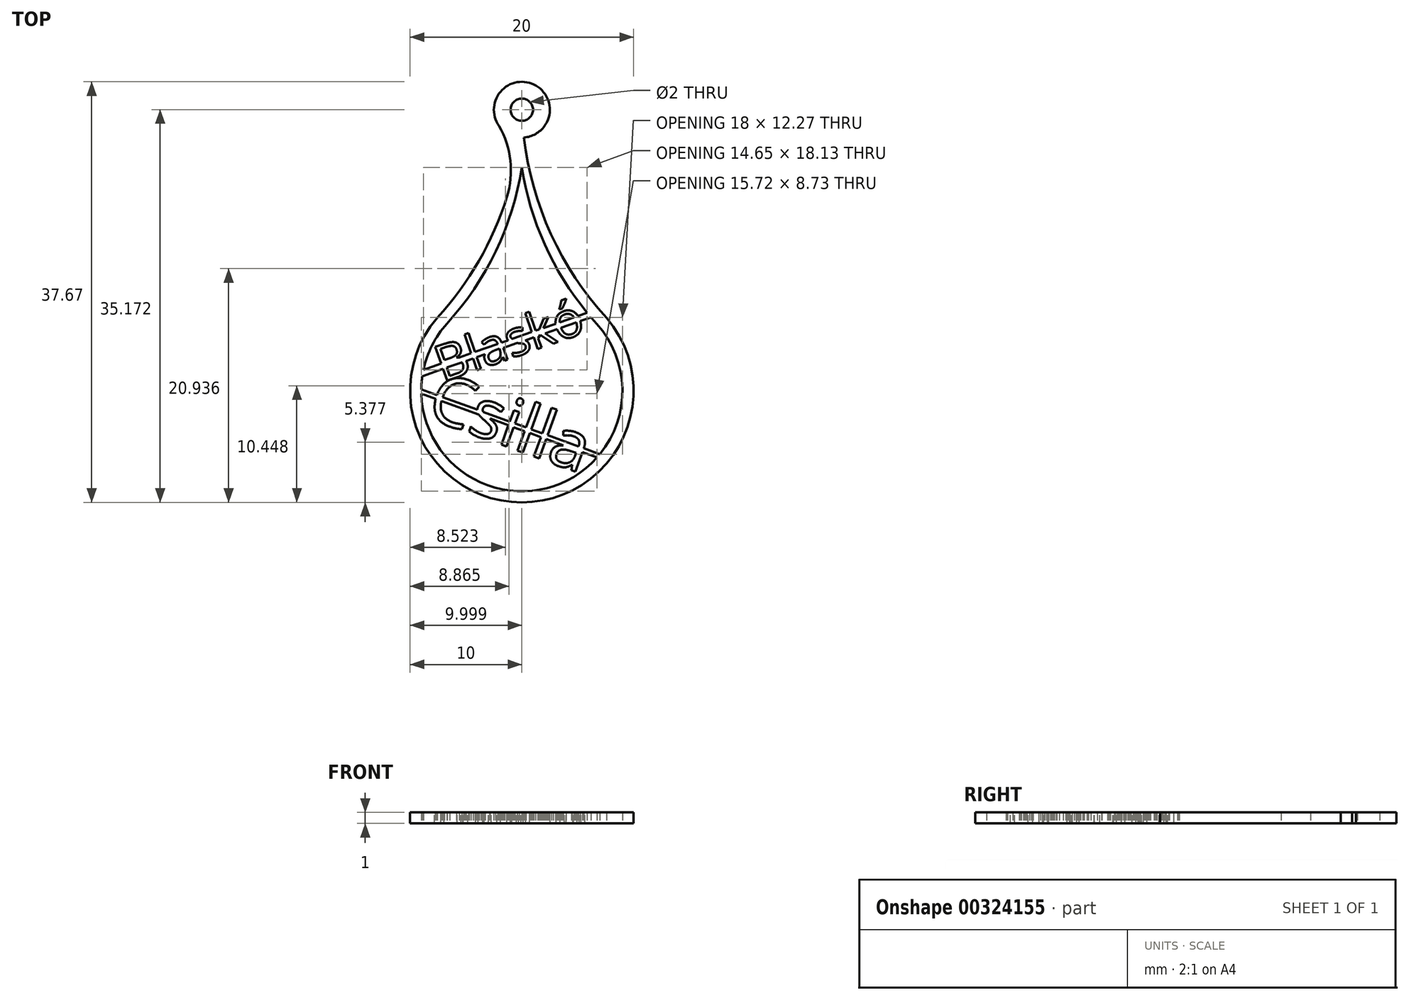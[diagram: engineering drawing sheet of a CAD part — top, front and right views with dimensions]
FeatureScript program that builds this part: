
annotation { "Feature Type Name" : "Feature", "Feature Type Description" : "" }
export const myFeature = defineFeature(function(context is Context, id is Id, definition is map)
    precondition{}
    {
        {
            var Q0;
            Q0=qCreatedBy(makeId("Top.planeOp"),FACE);
            var sketch = newSketch(context, id + "F0", { "sketchPlane" : qUnion([Q0])});
            skArc(sketch, "E0", {"start": v(-6.7, 6) * mm, "mid": v(-8.22, -3.67) * mm, "end": v(0, -9) * mm});
            skArc(sketch, "E1", {"start": v(-7.57, 6.53) * mm, "mid": v(-9.1, -4.16) * mm, "end": v(0, -10) * mm});
            skArc(sketch, "E2", {"start": v(-7.57, 6.53) * mm, "mid": v(-2.31, 14.71) * mm, "end": v(-0.05, 24.17) * mm});
            skLineSegment(sketch, "E3", {"start": v(0, 26.17) * mm, "end": v(0, -10) * mm, "construction": true});
            skArc(sketch, "E4", {"start": v(-6.7, 6) * mm, "mid": v(-2.33, 12.5) * mm, "end": v(0, 20) * mm});
            skArc(sketch, "E5.MirrorCS", {"start": v(0, 25.17) * mm, "mid": v(-0.01, 25.67) * mm, "end": v(-0.01, 26.17) * mm});
            skPoint(sketch, "E6", {"position": v(-8.16, 3.8) * mm});
            skLineSegment(sketch, "E7", {"start": v(0, 0) * mm, "end": v(-8.16, 3.8) * mm, "construction": true});
            skPoint(sketch, "E8.MirrorCS.end.orphan", {"position": v(0, 20) * mm});
            skPoint(sketch, "E9.MirrorCS.end.orphan", {"position": v(0, -9) * mm});
            skPoint(sketch, "E10.MirrorCS.end.orphan", {"position": v(0, -10) * mm});
            skArc(sketch, "E11.MirrorCS", {"start": v(6.7, 6) * mm, "mid": v(2.33, 12.5) * mm, "end": v(0, 20) * mm});
            skArc(sketch, "E12.MirrorCS", {"start": v(7.57, 6.53) * mm, "mid": v(1.93, 15.64) * mm, "end": v(-0.01, 26.17) * mm});
            skArc(sketch, "E13.MirrorCS", {"start": v(6.7, 6) * mm, "mid": v(8.22, -3.67) * mm, "end": v(0, -9) * mm});
            skArc(sketch, "E14.MirrorCS", {"start": v(7.57, 6.53) * mm, "mid": v(9.1, -4.16) * mm, "end": v(0, -10) * mm});
            skLineSegment(sketch, "E15", {"start": v(0, 0) * mm, "end": v(7.1, -10.14) * mm, "construction": true});
            skPoint(sketch, "E16", {"position": v(5.16, -7.37) * mm});
            skLineSegment(sketch, "E17", {"start": v(0, 0) * mm, "end": v(7.3, 12.66) * mm, "construction": true});
            skPoint(sketch, "E18", {"position": v(4.81, 8.33) * mm});
            skText(sketch, "E19", { "text": "Blaskó", "fontName": "OpenSans-Regular.ttf"});
            skText(sketch, "E20", { "text": "Csilla", "fontName": "OpenSans-Regular.ttf"});
            skLineSegment(sketch, "E21", {"start": v(0, 0) * mm, "end": v(-15.9, -4.26) * mm, "construction": true});
            skPoint(sketch, "E22", {"position": v(-8.7, -2.33) * mm});
            skLineSegment(sketch, "E23", {"start": v(-7.63, 2.28) * mm, "end": v(5.34, 6.81) * mm});
            skLineSegment(sketch, "E24", {"start": v(5.34, 6.81) * mm, "end": v(5.85, 7) * mm});
            skLineSegment(sketch, "E25", {"start": v(-7.63, 2.28) * mm, "end": v(-8.8, 1.87) * mm});
            skLineSegment(sketch, "E26", {"start": v(-8.9, 1.3) * mm, "end": v(6.2, 6.58) * mm});
            skLineSegment(sketch, "E27", {"start": v(-7.94, -0.26) * mm, "end": v(5.92, -5.3) * mm});
            skLineSegment(sketch, "E28", {"start": v(5.92, -5.3) * mm, "end": v(6.98, -5.69) * mm});
            skLineSegment(sketch, "E29", {"start": v(-7.94, -0.26) * mm, "end": v(-9, 0.13) * mm});
            skLineSegment(sketch, "E30", {"start": v(-9, -0.26) * mm, "end": v(6.73, -5.98) * mm});
            skCircle(sketch, "E31", {"center": v(0, 25.17) * mm, "radius": 1 * mm});
            skCircle(sketch, "E32", {"center": v(0, 25.17) * mm, "radius": 2.5 * mm});
            skArc(sketch, "E33", {"start": v(2.24, 24.06) * mm, "mid": v(1.06, 20.82) * mm, "end": v(1.33, 17.37) * mm});
            skArc(sketch, "E34.MirrorCS", {"start": v(-2.24, 24.06) * mm, "mid": v(-1.06, 20.82) * mm, "end": v(-1.33, 17.37) * mm});
            skArc(sketch, "E35.trimOffspring", {"start": v(0, 25.17) * mm, "mid": v(0.01, 25.67) * mm, "end": v(0.01, 26.17) * mm});
            skPoint(sketch, "E36.orphan", {"position": v(0, 27) * mm});
            skArc(sketch, "E37.trimOffspring", {"start": v(0, 27) * mm, "mid": v(0, 27) * mm, "end": v(0, 27) * mm});
            const initialGuessF0  = {"E19": [-0.0071, 0.00076, 0.94407, 0.32975, 0.00322], "E20": [-0.0087, -0.00233, 0.9397, -0.34202, 0.00441]};
            skSetInitialGuess(sketch, initialGuessF0);
            skSolve(sketch);
        }
        {
            var Q0;
            Q0=makeQuery(id+"F0.imprint","IMPRINT",FACE,{"disambiguationData":[TD([[makeQuery(id+"F0.imprint","IMPRINT",EDGE,{"derivedFrom":sQuery(id+"F0.wireOp",EDGE,"E0")}),-1.0]])]});
            var Q1;
            Q1=makeQuery(id+"F0.imprint","IMPRINT",FACE,{"disambiguationData":[TD([[makeQuery(id+"F0.imprint","IMPRINT",EDGE,{"derivedFrom":sQuery(id+"F0.wireOp",EDGE,"E19.sketch_text.stroke-56")}),-1.0]])]});
            var Q2;
            Q2=makeQuery(id+"F0.imprint","IMPRINT",FACE,{"disambiguationData":[TD([[makeQuery(id+"F0.imprint","IMPRINT",EDGE,{"derivedFrom":sQuery(id+"F0.wireOp",EDGE,"E19.sketch_text.stroke-81")}),-1.0]])]});
            var Q3;
            Q3=makeQuery(id+"F0.imprint","IMPRINT",FACE,{"disambiguationData":[TD([[makeQuery(id+"F0.imprint","IMPRINT",EDGE,{"derivedFrom":sQuery(id+"F0.wireOp",EDGE,"E19.sketch_text.stroke-96")}),-1.0]])]});
            var Q4;
            Q4=makeQuery(id+"F0.imprint","IMPRINT",FACE,{"disambiguationData":[TD([[makeQuery(id+"F0.imprint","IMPRINT",EDGE,{"derivedFrom":sQuery(id+"F0.wireOp",EDGE,"E19.sketch_text.stroke-113")}),-1.0]])]});
            var Q5;
            Q5=makeQuery(id+"F0.imprint","IMPRINT",FACE,{"disambiguationData":[TD([[makeQuery(id+"F0.imprint","IMPRINT",EDGE,{"derivedFrom":sQuery(id+"F0.wireOp",EDGE,"E19.sketch_text.stroke-29")}),-1.0]])]});
            var Q6;
            Q6=makeQuery(id+"F0.imprint","IMPRINT",FACE,{"disambiguationData":[TD([[makeQuery(id+"F0.imprint","IMPRINT",EDGE,{"derivedFrom":sQuery(id+"F0.wireOp",EDGE,"E19.sketch_text.stroke-25")}),-1.0]])]});
            var Q7;
            Q7=makeQuery(id+"F0.imprint","IMPRINT",FACE,{"disambiguationData":[TD([[makeQuery(id+"F0.imprint","IMPRINT",EDGE,{"derivedFrom":sQuery(id+"F0.wireOp",EDGE,"E19.sketch_text.stroke-0")}),-1.0]])]});
            var Q8;
            Q8=makeQuery(id+"F0.imprint","IMPRINT",FACE,{"disambiguationData":[TD([[makeQuery(id+"F0.imprint","IMPRINT",EDGE,{"derivedFrom":sQuery(id+"F0.wireOp",EDGE,"E20.sketch_text.stroke-0")}),-1.0]])]});
            var Q9;
            Q9=makeQuery(id+"F0.imprint","IMPRINT",FACE,{"disambiguationData":[TD([[makeQuery(id+"F0.imprint","IMPRINT",EDGE,{"derivedFrom":sQuery(id+"F0.wireOp",EDGE,"E20.sketch_text.stroke-15")}),-1.0]])]});
            var Q10;
            Q10=makeQuery(id+"F0.imprint","IMPRINT",FACE,{"disambiguationData":[TD([[makeQuery(id+"F0.imprint","IMPRINT",EDGE,{"derivedFrom":sQuery(id+"F0.wireOp",EDGE,"E20.sketch_text.stroke-44")}),-1.0]])]});
            var Q11;
            Q11=makeQuery(id+"F0.imprint","IMPRINT",FACE,{"disambiguationData":[TD([[makeQuery(id+"F0.imprint","IMPRINT",EDGE,{"derivedFrom":sQuery(id+"F0.wireOp",EDGE,"E20.sketch_text.stroke-52")}),-1.0]])]});
            var Q12;
            Q12=makeQuery(id+"F0.imprint","IMPRINT",FACE,{"disambiguationData":[TD([[makeQuery(id+"F0.imprint","IMPRINT",EDGE,{"derivedFrom":sQuery(id+"F0.wireOp",EDGE,"E20.sketch_text.stroke-40")}),-1.0]])]});
            var Q13;
            Q13=makeQuery(id+"F0.imprint","IMPRINT",FACE,{"disambiguationData":[TD([[makeQuery(id+"F0.imprint","IMPRINT",EDGE,{"derivedFrom":sQuery(id+"F0.wireOp",EDGE,"E20.sketch_text.stroke-56")}),-1.0]])]});
            var Q14;
            Q14=makeQuery(id+"F0.imprint","IMPRINT",FACE,{"disambiguationData":[TD([[makeQuery(id+"F0.imprint","IMPRINT",EDGE,{"derivedFrom":sQuery(id+"F0.wireOp",EDGE,"E20.sketch_text.stroke-60")}),-1.0]])]});
            var Q15;
            {var subQ0=sQuery(id+"F0.wireOp",EDGE,"E20.sketch_text.stroke-26");Q15=makeQuery(id+"F0.imprint","IMPRINT",FACE,{"disambiguationData":[TD([[makeQuery(id+"F0.imprint","IMPRINT",EDGE,{"derivedFrom":subQ0}),1.0]])]});}
            var Q16;
            {var subQ0=sQuery(id+"F0.wireOp",EDGE,"E29");Q16=makeQuery(id+"F0.imprint","IMPRINT",FACE,{"disambiguationData":[TD([[makeQuery(id+"F0.imprint","IMPRINT",EDGE,{"derivedFrom":subQ0}),1.0]])]});}
            var Q17;
            {var subQ5=sQuery(id+"F0.wireOp",EDGE,"E20.sketch_text.stroke-2");var subQ6=sQuery(id+"F0.wireOp",EDGE,"E20.sketch_text.stroke-1");var subQ7=makeQuery(id+"F0.imprint","INTERSECT",VERTEX,{"derivedFrom":[subQ6,subQ5]});Q17=makeQuery(id+"F0.imprint","IMPRINT",FACE,{"disambiguationData":[TD([[makeQuery(id+"F0.imprint","IMPRINT",EDGE,{"disambiguationData":[TD([[subQ7,1.0]])],"derivedFrom":subQ6}),-1.0]])]});}
            var Q18;
            {var subQ0=sQuery(id+"F0.wireOp",EDGE,"E20.sketch_text.stroke-3");Q18=makeQuery(id+"F0.imprint","IMPRINT",FACE,{"disambiguationData":[TD([[makeQuery(id+"F0.imprint","IMPRINT",EDGE,{"derivedFrom":subQ0}),-1.0]])]});}
            var Q19;
            {var subQ5=sQuery(id+"F0.wireOp",EDGE,"E20.sketch_text.stroke-26");Q19=makeQuery(id+"F0.imprint","IMPRINT",FACE,{"disambiguationData":[TD([[makeQuery(id+"F0.imprint","IMPRINT",EDGE,{"derivedFrom":subQ5}),-1.0]])]});}
            var Q20;
            {var subQ6=sQuery(id+"F0.wireOp",EDGE,"E20.sketch_text.stroke-28");Q20=makeQuery(id+"F0.imprint","IMPRINT",FACE,{"disambiguationData":[TD([[makeQuery(id+"F0.imprint","IMPRINT",EDGE,{"derivedFrom":subQ6}),-1.0]])]});}
            var Q21;
            {var subQ6=sQuery(id+"F0.wireOp",EDGE,"E20.sketch_text.stroke-37");Q21=makeQuery(id+"F0.imprint","IMPRINT",FACE,{"disambiguationData":[TD([[makeQuery(id+"F0.imprint","IMPRINT",EDGE,{"derivedFrom":subQ6}),1.0]])]});}
            var Q22;
            {var subQ0=sQuery(id+"F0.wireOp",EDGE,"E30");var subQ1=sQuery(id+"F0.wireOp",EDGE,"E20.sketch_text.stroke-41");var subQ2=makeQuery(id+"F0.imprint","INTERSECT",VERTEX,{"derivedFrom":[subQ1,subQ0]});Q22=makeQuery(id+"F0.imprint","IMPRINT",FACE,{"disambiguationData":[TD([[makeQuery(id+"F0.imprint","IMPRINT",EDGE,{"disambiguationData":[TD([[subQ2,-1.0]])],"derivedFrom":subQ1}),-1.0]])]});}
            var Q23;
            {var subQ0=sQuery(id+"F0.wireOp",EDGE,"E20.sketch_text.stroke-42");Q23=makeQuery(id+"F0.imprint","IMPRINT",FACE,{"disambiguationData":[TD([[makeQuery(id+"F0.imprint","IMPRINT",EDGE,{"derivedFrom":subQ0}),-1.0]])]});}
            var Q24;
            {var subQ0=sQuery(id+"F0.wireOp",EDGE,"E27");var subQ1=sQuery(id+"F0.wireOp",EDGE,"E20.sketch_text.stroke-43");var subQ2=makeQuery(id+"F0.imprint","INTERSECT",VERTEX,{"derivedFrom":[subQ1,subQ0]});Q24=makeQuery(id+"F0.imprint","IMPRINT",FACE,{"disambiguationData":[TD([[makeQuery(id+"F0.imprint","IMPRINT",EDGE,{"disambiguationData":[TD([[subQ2,-1.0]])],"derivedFrom":subQ1}),1.0]])]});}
            var Q25;
            {var subQ0=sQuery(id+"F0.wireOp",EDGE,"E30");var subQ1=sQuery(id+"F0.wireOp",EDGE,"E20.sketch_text.stroke-53");var subQ2=makeQuery(id+"F0.imprint","INTERSECT",VERTEX,{"derivedFrom":[subQ1,subQ0]});Q25=makeQuery(id+"F0.imprint","IMPRINT",FACE,{"disambiguationData":[TD([[makeQuery(id+"F0.imprint","IMPRINT",EDGE,{"disambiguationData":[TD([[subQ2,-1.0]])],"derivedFrom":subQ1}),-1.0]])]});}
            var Q26;
            {var subQ0=sQuery(id+"F0.wireOp",EDGE,"E20.sketch_text.stroke-54");Q26=makeQuery(id+"F0.imprint","IMPRINT",FACE,{"disambiguationData":[TD([[makeQuery(id+"F0.imprint","IMPRINT",EDGE,{"derivedFrom":subQ0}),-1.0]])]});}
            var Q27;
            {var subQ0=sQuery(id+"F0.wireOp",EDGE,"E27");var subQ1=sQuery(id+"F0.wireOp",EDGE,"E20.sketch_text.stroke-55");var subQ2=makeQuery(id+"F0.imprint","INTERSECT",VERTEX,{"derivedFrom":[subQ1,subQ0]});Q27=makeQuery(id+"F0.imprint","IMPRINT",FACE,{"disambiguationData":[TD([[makeQuery(id+"F0.imprint","IMPRINT",EDGE,{"disambiguationData":[TD([[subQ2,-1.0]])],"derivedFrom":subQ1}),1.0]])]});}
            var Q28;
            {var subQ0=sQuery(id+"F0.wireOp",EDGE,"E20.sketch_text.stroke-58");Q28=makeQuery(id+"F0.imprint","IMPRINT",FACE,{"disambiguationData":[TD([[makeQuery(id+"F0.imprint","IMPRINT",EDGE,{"derivedFrom":subQ0}),-1.0]])]});}
            var Q29;
            {var subQ0=sQuery(id+"F0.wireOp",EDGE,"E30");var subQ1=sQuery(id+"F0.wireOp",EDGE,"E20.sketch_text.stroke-57");var subQ2=makeQuery(id+"F0.imprint","INTERSECT",VERTEX,{"derivedFrom":[subQ1,subQ0]});Q29=makeQuery(id+"F0.imprint","IMPRINT",FACE,{"disambiguationData":[TD([[makeQuery(id+"F0.imprint","IMPRINT",EDGE,{"disambiguationData":[TD([[subQ2,-1.0]])],"derivedFrom":subQ1}),-1.0]])]});}
            var Q30;
            {var subQ6=sQuery(id+"F0.wireOp",EDGE,"E20.sketch_text.stroke-67");Q30=makeQuery(id+"F0.imprint","IMPRINT",FACE,{"disambiguationData":[TD([[makeQuery(id+"F0.imprint","IMPRINT",EDGE,{"derivedFrom":subQ6}),1.0]])]});}
            var Q31;
            {var subQ0=sQuery(id+"F0.wireOp",EDGE,"E20.sketch_text.stroke-70");Q31=makeQuery(id+"F0.imprint","IMPRINT",FACE,{"disambiguationData":[TD([[makeQuery(id+"F0.imprint","IMPRINT",EDGE,{"derivedFrom":subQ0}),-1.0]])]});}
            var Q32;
            {var subQ10=sQuery(id+"F0.wireOp",EDGE,"E20.sketch_text.stroke-67");Q32=makeQuery(id+"F0.imprint","IMPRINT",FACE,{"disambiguationData":[TD([[makeQuery(id+"F0.imprint","IMPRINT",EDGE,{"derivedFrom":subQ10}),-1.0]])]});}
            var Q33;
            {var subQ0=sQuery(id+"F0.wireOp",EDGE,"E28");Q33=makeQuery(id+"F0.imprint","IMPRINT",FACE,{"disambiguationData":[TD([[makeQuery(id+"F0.imprint","IMPRINT",EDGE,{"derivedFrom":subQ0}),-1.0]])]});}
            var Q34;
            {var subQ0=sQuery(id+"F0.wireOp",EDGE,"E25");Q34=makeQuery(id+"F0.imprint","IMPRINT",FACE,{"disambiguationData":[TD([[makeQuery(id+"F0.imprint","IMPRINT",EDGE,{"derivedFrom":subQ0}),1.0]])]});}
            var Q35;
            {var subQ0=sQuery(id+"F0.wireOp",EDGE,"E19.sketch_text.stroke-23");Q35=makeQuery(id+"F0.imprint","IMPRINT",FACE,{"disambiguationData":[TD([[makeQuery(id+"F0.imprint","IMPRINT",EDGE,{"derivedFrom":subQ0}),-1.0]])]});}
            var Q36;
            {var subQ10=sQuery(id+"F0.wireOp",EDGE,"E19.sketch_text.stroke-7");Q36=makeQuery(id+"F0.imprint","IMPRINT",FACE,{"disambiguationData":[TD([[makeQuery(id+"F0.imprint","IMPRINT",EDGE,{"derivedFrom":subQ10}),-1.0]])]});}
            var Q37;
            {var subQ1=sQuery(id+"F0.wireOp",EDGE,"E19.sketch_text.stroke-23");Q37=makeQuery(id+"F0.imprint","IMPRINT",FACE,{"disambiguationData":[TD([[makeQuery(id+"F0.imprint","IMPRINT",EDGE,{"derivedFrom":subQ1}),1.0]])]});}
            var Q38;
            {var subQ0=sQuery(id+"F0.wireOp",EDGE,"E23");var subQ1=sQuery(id+"F0.wireOp",EDGE,"E19.sketch_text.stroke-6");var subQ2=makeQuery(id+"F0.imprint","INTERSECT",VERTEX,{"derivedFrom":[subQ1,subQ0]});Q38=makeQuery(id+"F0.imprint","IMPRINT",FACE,{"disambiguationData":[TD([[makeQuery(id+"F0.imprint","IMPRINT",EDGE,{"disambiguationData":[TD([[subQ2,-1.0]])],"derivedFrom":subQ1}),1.0]])]});}
            var Q39;
            {var subQ0=sQuery(id+"F0.wireOp",EDGE,"E26");var subQ1=sQuery(id+"F0.wireOp",EDGE,"E19.sketch_text.stroke-26");var subQ2=makeQuery(id+"F0.imprint","INTERSECT",VERTEX,{"derivedFrom":[subQ1,subQ0]});Q39=makeQuery(id+"F0.imprint","IMPRINT",FACE,{"disambiguationData":[TD([[makeQuery(id+"F0.imprint","IMPRINT",EDGE,{"disambiguationData":[TD([[subQ2,-1.0]])],"derivedFrom":subQ1}),-1.0]])]});}
            var Q40;
            {var subQ0=sQuery(id+"F0.wireOp",EDGE,"E19.sketch_text.stroke-27");Q40=makeQuery(id+"F0.imprint","IMPRINT",FACE,{"disambiguationData":[TD([[makeQuery(id+"F0.imprint","IMPRINT",EDGE,{"derivedFrom":subQ0}),-1.0]])]});}
            var Q41;
            {var subQ6=sQuery(id+"F0.wireOp",EDGE,"E19.sketch_text.stroke-36");Q41=makeQuery(id+"F0.imprint","IMPRINT",FACE,{"disambiguationData":[TD([[makeQuery(id+"F0.imprint","IMPRINT",EDGE,{"derivedFrom":subQ6}),1.0]])]});}
            var Q42;
            {var subQ14=sQuery(id+"F0.wireOp",EDGE,"E19.sketch_text.stroke-36");Q42=makeQuery(id+"F0.imprint","IMPRINT",FACE,{"disambiguationData":[TD([[makeQuery(id+"F0.imprint","IMPRINT",EDGE,{"derivedFrom":subQ14}),-1.0]])]});}
            var Q43;
            {var subQ5=sQuery(id+"F0.wireOp",EDGE,"E19.sketch_text.stroke-39");Q43=makeQuery(id+"F0.imprint","IMPRINT",FACE,{"disambiguationData":[TD([[makeQuery(id+"F0.imprint","IMPRINT",EDGE,{"derivedFrom":subQ5}),-1.0]])]});}
            var Q44;
            {var subQ0=sQuery(id+"F0.wireOp",EDGE,"E19.sketch_text.stroke-66");Q44=makeQuery(id+"F0.imprint","IMPRINT",FACE,{"disambiguationData":[TD([[makeQuery(id+"F0.imprint","IMPRINT",EDGE,{"derivedFrom":subQ0}),1.0]])]});}
            var Q45;
            {var subQ7=sQuery(id+"F0.wireOp",EDGE,"E19.sketch_text.stroke-66");Q45=makeQuery(id+"F0.imprint","IMPRINT",FACE,{"disambiguationData":[TD([[makeQuery(id+"F0.imprint","IMPRINT",EDGE,{"derivedFrom":subQ7}),-1.0]])]});}
            var Q46;
            {var subQ6=sQuery(id+"F0.wireOp",EDGE,"E19.sketch_text.stroke-69");Q46=makeQuery(id+"F0.imprint","IMPRINT",FACE,{"disambiguationData":[TD([[makeQuery(id+"F0.imprint","IMPRINT",EDGE,{"derivedFrom":subQ6}),-1.0]])]});}
            var Q47;
            {var subQ1=sQuery(id+"F0.wireOp",EDGE,"E19.sketch_text.stroke-78");Q47=makeQuery(id+"F0.imprint","IMPRINT",FACE,{"disambiguationData":[TD([[makeQuery(id+"F0.imprint","IMPRINT",EDGE,{"derivedFrom":subQ1}),1.0]])]});}
            var Q48;
            {var subQ4=sQuery(id+"F0.wireOp",EDGE,"E19.sketch_text.stroke-89");Q48=makeQuery(id+"F0.imprint","IMPRINT",FACE,{"disambiguationData":[TD([[makeQuery(id+"F0.imprint","IMPRINT",EDGE,{"derivedFrom":subQ4}),-1.0]])]});}
            var Q49;
            {var subQ0=sQuery(id+"F0.wireOp",EDGE,"E19.sketch_text.stroke-92");Q49=makeQuery(id+"F0.imprint","IMPRINT",FACE,{"disambiguationData":[TD([[makeQuery(id+"F0.imprint","IMPRINT",EDGE,{"derivedFrom":subQ0}),-1.0]])]});}
            var Q50;
            {var subQ0=sQuery(id+"F0.wireOp",EDGE,"E19.sketch_text.stroke-83");Q50=makeQuery(id+"F0.imprint","IMPRINT",FACE,{"disambiguationData":[TD([[makeQuery(id+"F0.imprint","IMPRINT",EDGE,{"derivedFrom":subQ0}),-1.0]])]});}
            var Q51;
            {var subQ5=sQuery(id+"F0.wireOp",EDGE,"E19.sketch_text.stroke-85");var subQ6=sQuery(id+"F0.wireOp",EDGE,"E19.sketch_text.stroke-84");var subQ7=makeQuery(id+"F0.imprint","INTERSECT",VERTEX,{"derivedFrom":[subQ6,subQ5]});Q51=makeQuery(id+"F0.imprint","IMPRINT",FACE,{"disambiguationData":[TD([[makeQuery(id+"F0.imprint","IMPRINT",EDGE,{"disambiguationData":[TD([[subQ7,1.0]])],"derivedFrom":subQ6}),1.0]])]});}
            var Q52;
            {var subQ0=sQuery(id+"F0.wireOp",EDGE,"E19.sketch_text.stroke-86");Q52=makeQuery(id+"F0.imprint","IMPRINT",FACE,{"disambiguationData":[TD([[makeQuery(id+"F0.imprint","IMPRINT",EDGE,{"derivedFrom":subQ0}),-1.0]])]});}
            var Q53;
            {var subQ7=sQuery(id+"F0.wireOp",EDGE,"E19.sketch_text.stroke-101");var subQ8=sQuery(id+"F0.wireOp",EDGE,"E19.sketch_text.stroke-100");var subQ9=makeQuery(id+"F0.imprint","INTERSECT",VERTEX,{"derivedFrom":[subQ8,subQ7]});Q53=makeQuery(id+"F0.imprint","IMPRINT",FACE,{"disambiguationData":[TD([[makeQuery(id+"F0.imprint","IMPRINT",EDGE,{"disambiguationData":[TD([[subQ9,1.0]])],"derivedFrom":subQ8}),-1.0]])]});}
            var Q54;
            {var subQ6=sQuery(id+"F0.wireOp",EDGE,"E19.sketch_text.stroke-102");Q54=makeQuery(id+"F0.imprint","IMPRINT",FACE,{"disambiguationData":[TD([[makeQuery(id+"F0.imprint","IMPRINT",EDGE,{"derivedFrom":subQ6}),-1.0]])]});}
            var Q55;
            {var subQ0=sQuery(id+"F0.wireOp",EDGE,"E19.sketch_text.stroke-112");var subQ1=sQuery(id+"F0.wireOp",EDGE,"E19.sketch_text.stroke-105");var subQ2=makeQuery(id+"F0.imprint","INTERSECT",VERTEX,{"derivedFrom":[subQ1,subQ0]});Q55=makeQuery(id+"F0.imprint","IMPRINT",FACE,{"disambiguationData":[TD([[makeQuery(id+"F0.imprint","IMPRINT",EDGE,{"disambiguationData":[TD([[subQ2,-1.0]])],"derivedFrom":subQ1}),1.0]])]});}
            var Q56;
            {var subQ7=sQuery(id+"F0.wireOp",EDGE,"E19.sketch_text.stroke-97");Q56=makeQuery(id+"F0.imprint","IMPRINT",FACE,{"disambiguationData":[TD([[makeQuery(id+"F0.imprint","IMPRINT",EDGE,{"derivedFrom":subQ7}),-1.0]])]});}
            var Q57;
            {var subQ5=sQuery(id+"F0.wireOp",EDGE,"E24");Q57=makeQuery(id+"F0.imprint","IMPRINT",FACE,{"disambiguationData":[TD([[makeQuery(id+"F0.imprint","IMPRINT",EDGE,{"derivedFrom":subQ5}),-1.0]])]});}
            var Q58;
            {var subQ0=sQuery(id+"F0.wireOp",EDGE,"E32");var subQ5=sQuery(id+"F0.wireOp",EDGE,"E2");var subQ6=makeQuery(id+"F0.imprint","INTERSECT",VERTEX,{"derivedFrom":[subQ5,subQ0]});Q58=makeQuery(id+"F0.imprint","IMPRINT",FACE,{"disambiguationData":[TD([[makeQuery(id+"F0.imprint","IMPRINT",EDGE,{"disambiguationData":[TD([[subQ6,-1.0]])],"derivedFrom":subQ5}),1.0]])]});}
            var Q59;
            {var subQ0=sQuery(id+"F0.wireOp",EDGE,"E32");var subQ1=sQuery(id+"F0.wireOp",EDGE,"E2");var subQ2=makeQuery(id+"F0.imprint","INTERSECT",VERTEX,{"derivedFrom":[subQ1,subQ0]});Q59=makeQuery(id+"F0.imprint","IMPRINT",FACE,{"disambiguationData":[TD([[makeQuery(id+"F0.imprint","IMPRINT",EDGE,{"disambiguationData":[TD([[subQ2,-1.0]])],"derivedFrom":subQ1}),-1.0]])]});}
            var Q60;
            {var subQ0=sQuery(id+"F0.wireOp",EDGE,"E33");var subQ1=sQuery(id+"F0.wireOp",EDGE,"E12.MirrorCS");var subQ2=makeQuery(id+"F0.imprint","INTERSECT",VERTEX,{"derivedFrom":[subQ1,subQ0]});Q60=makeQuery(id+"F0.imprint","IMPRINT",FACE,{"disambiguationData":[TD([[makeQuery(id+"F0.imprint","IMPRINT",EDGE,{"disambiguationData":[TD([[subQ2,-1.0]])],"derivedFrom":subQ1}),-1.0]])]});}
            var Q61;
            {var subQ0=sQuery(id+"F0.wireOp",EDGE,"E34.MirrorCS");var subQ1=sQuery(id+"F0.wireOp",EDGE,"E2");var subQ2=makeQuery(id+"F0.imprint","INTERSECT",VERTEX,{"derivedFrom":[subQ1,subQ0]});Q61=makeQuery(id+"F0.imprint","IMPRINT",FACE,{"disambiguationData":[TD([[makeQuery(id+"F0.imprint","IMPRINT",EDGE,{"disambiguationData":[TD([[subQ2,-1.0]])],"derivedFrom":subQ1}),1.0]])]});}
            var Q62;
            {var subQ2=sQuery(id+"F0.wireOp",EDGE,"E19.sketch_text.stroke-81");Q62=makeQuery(id+"F0.imprint","IMPRINT",FACE,{"disambiguationData":[TD([[makeQuery(id+"F0.imprint","IMPRINT",EDGE,{"derivedFrom":subQ2}),1.0]])]});}
            extrude(context, id + "F1", {"entities" : qUnion([Q0, Q1, Q2, Q3, Q4, Q5, Q6, Q7, Q8, Q9, Q10, Q11, Q12, Q13, Q14, Q15, Q16, Q17, Q18, Q19, Q20, Q21, Q22, Q23, Q24, Q25, Q26, Q27, Q28, Q29, Q30, Q31, Q32, Q33, Q34, Q35, Q36, Q37, Q38, Q39, Q40, Q41, Q42, Q43, Q44, Q45, Q46, Q47, Q48, Q49, Q50, Q51, Q52, Q53, Q54, Q55, Q56, Q57, Q58, Q59, Q60, Q61, Q62]), "depth" : 1 * mm});
        }
    });
